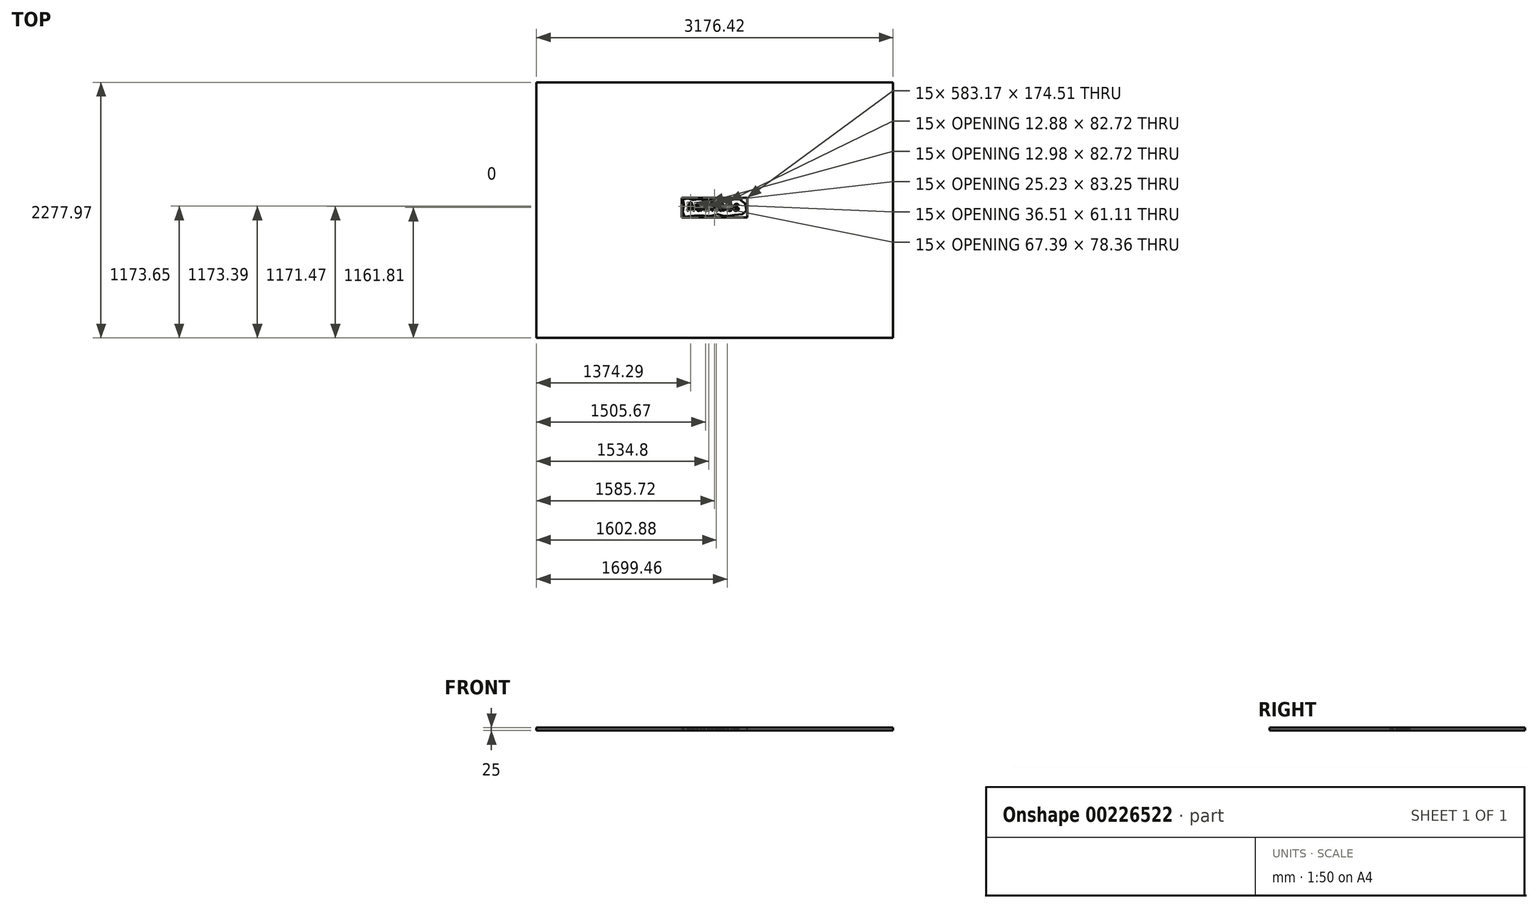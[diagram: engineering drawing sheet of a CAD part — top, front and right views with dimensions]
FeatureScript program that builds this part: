
annotation { "Feature Type Name" : "Feature", "Feature Type Description" : "" }
export const myFeature = defineFeature(function(context is Context, id is Id, definition is map)
    precondition{}
    {
        {
            var Q0;
            Q0=qCreatedBy(makeId("Top.planeOp"),FACE);
            var sketch = newSketch(context, id + "F0", { "sketchPlane" : qUnion([Q0])});
            skLineSegment(sketch, "E0.bottom", {"start": v(0, 0) * mm, "end": v(583.17, 0) * mm});
            skLineSegment(sketch, "E0.top", {"start": v(0, 174.5) * mm, "end": v(583.17, 174.5) * mm});
            skLineSegment(sketch, "E0.left", {"start": v(0, 0) * mm, "end": v(0, 174.5) * mm});
            skLineSegment(sketch, "E0.right", {"start": v(583.17, 0) * mm, "end": v(583.17, 174.5) * mm});
            skSolve(sketch);
        }
        {
            var Q0;
            Q0=qCreatedBy(makeId("Top.planeOp"),FACE);
            var sketch = newSketch(context, id + "F1", { "sketchPlane" : qUnion([Q0])});
            skText(sketch, "E1", { "text": "Audilabs", "fontName": "AllertaStencil-Regular.ttf"});
            const initialGuessF1  = {"E1": [0.03974, 0.05773, 1, 0, 0.0785]};
            skSetInitialGuess(sketch, initialGuessF1);
            skSolve(sketch);
        }
        {
            var Q0;
            Q0=makeQuery(id+"F0.imprint","IMPRINT",FACE,{"disambiguationData":[TD([[makeQuery(id+"F0.imprint","IMPRINT",EDGE,{"derivedFrom":sQuery(id+"F0.wireOp",EDGE,"E0.bottom")}),1.0]])]});
            extrude(context, id + "F2", {"entities" : qUnion([Q0]), "depth" : 25 * mm});
        }
        {
            var Q0;
            Q0 = qSketchRegion(id + "F1", true);
            var Q1;
            Q1=makeQuery(id+"F1.imprint","IMPRINT",FACE,{"disambiguationData":[TD([[makeQuery(id+"F1.imprint","IMPRINT",EDGE,{"derivedFrom":sQuery(id+"F1.wireOp",EDGE,"E1.sketch_text.stroke-213")}),-1.0]])]});
            var Q2;
            Q2=makeQuery(id+"F1.imprint","IMPRINT",FACE,{"disambiguationData":[TD([[makeQuery(id+"F1.imprint","IMPRINT",EDGE,{"derivedFrom":sQuery(id+"F1.wireOp",EDGE,"E1.sketch_text.stroke-204")}),-1.0]])]});
            var Q3;
            Q3=makeQuery(id+"F1.imprint","IMPRINT",FACE,{"disambiguationData":[TD([[makeQuery(id+"F1.imprint","IMPRINT",EDGE,{"derivedFrom":sQuery(id+"F1.wireOp",EDGE,"E1.sketch_text.stroke-184")}),-1.0]])]});
            var Q4;
            Q4=makeQuery(id+"F1.imprint","IMPRINT",FACE,{"disambiguationData":[TD([[makeQuery(id+"F1.imprint","IMPRINT",EDGE,{"derivedFrom":sQuery(id+"F1.wireOp",EDGE,"E1.sketch_text.stroke-198")}),-1.0]])]});
            var Q5;
            Q5=makeQuery(id+"F1.imprint","IMPRINT",FACE,{"disambiguationData":[TD([[makeQuery(id+"F1.imprint","IMPRINT",EDGE,{"derivedFrom":sQuery(id+"F1.wireOp",EDGE,"E1.sketch_text.stroke-0")}),-1.0]])]});
            var Q6;
            Q6=makeQuery(id+"F1.imprint","IMPRINT",FACE,{"disambiguationData":[TD([[makeQuery(id+"F1.imprint","IMPRINT",EDGE,{"derivedFrom":sQuery(id+"F1.wireOp",EDGE,"E1.sketch_text.stroke-7")}),-1.0]])]});
            var Q7;
            Q7=makeQuery(id+"F1.imprint","IMPRINT",FACE,{"disambiguationData":[TD([[makeQuery(id+"F1.imprint","IMPRINT",EDGE,{"derivedFrom":sQuery(id+"F1.wireOp",EDGE,"E1.sketch_text.stroke-11")}),-1.0]])]});
            var Q8;
            Q8=makeQuery(id+"F1.imprint","IMPRINT",FACE,{"disambiguationData":[TD([[makeQuery(id+"F1.imprint","IMPRINT",EDGE,{"derivedFrom":sQuery(id+"F1.wireOp",EDGE,"E1.sketch_text.stroke-31")}),-1.0]])]});
            var Q9;
            Q9=makeQuery(id+"F1.imprint","IMPRINT",FACE,{"disambiguationData":[TD([[makeQuery(id+"F1.imprint","IMPRINT",EDGE,{"derivedFrom":sQuery(id+"F1.wireOp",EDGE,"E1.sketch_text.stroke-36")}),-1.0]])]});
            var Q10;
            Q10=makeQuery(id+"F1.imprint","IMPRINT",FACE,{"disambiguationData":[TD([[makeQuery(id+"F1.imprint","IMPRINT",EDGE,{"derivedFrom":sQuery(id+"F1.wireOp",EDGE,"E1.sketch_text.stroke-41")}),-1.0]])]});
            var Q11;
            Q11=makeQuery(id+"F1.imprint","IMPRINT",FACE,{"disambiguationData":[TD([[makeQuery(id+"F1.imprint","IMPRINT",EDGE,{"derivedFrom":sQuery(id+"F1.wireOp",EDGE,"E1.sketch_text.stroke-66")}),-1.0]])]});
            var Q12;
            Q12=makeQuery(id+"F1.imprint","IMPRINT",FACE,{"disambiguationData":[TD([[makeQuery(id+"F1.imprint","IMPRINT",EDGE,{"derivedFrom":sQuery(id+"F1.wireOp",EDGE,"E1.sketch_text.stroke-70")}),-1.0]])]});
            var Q13;
            Q13=makeQuery(id+"F1.imprint","IMPRINT",FACE,{"disambiguationData":[TD([[makeQuery(id+"F1.imprint","IMPRINT",EDGE,{"derivedFrom":sQuery(id+"F1.wireOp",EDGE,"E1.sketch_text.stroke-78")}),-1.0]])]});
            var Q14;
            Q14=makeQuery(id+"F1.imprint","IMPRINT",FACE,{"disambiguationData":[TD([[makeQuery(id+"F1.imprint","IMPRINT",EDGE,{"derivedFrom":sQuery(id+"F1.wireOp",EDGE,"E1.sketch_text.stroke-96")}),-1.0]])]});
            var Q15;
            Q15=makeQuery(id+"F1.imprint","IMPRINT",FACE,{"disambiguationData":[TD([[makeQuery(id+"F1.imprint","IMPRINT",EDGE,{"derivedFrom":sQuery(id+"F1.wireOp",EDGE,"E1.sketch_text.stroke-115")}),-1.0]])]});
            var Q16;
            Q16=makeQuery(id+"F1.imprint","IMPRINT",FACE,{"disambiguationData":[TD([[makeQuery(id+"F1.imprint","IMPRINT",EDGE,{"derivedFrom":sQuery(id+"F1.wireOp",EDGE,"E1.sketch_text.stroke-151")}),-1.0]])]});
            var Q17;
            Q17=makeQuery(id+"F1.imprint","IMPRINT",FACE,{"disambiguationData":[TD([[makeQuery(id+"F1.imprint","IMPRINT",EDGE,{"derivedFrom":sQuery(id+"F1.wireOp",EDGE,"E1.sketch_text.stroke-157")}),-1.0]])]});
            extrude(context, id + "F3", {"entities" : qUnion([Q0, Q1, Q2, Q3, Q4, Q5, Q6, Q7, Q8, Q9, Q10, Q11, Q12, Q13, Q14, Q15, Q16, Q17]), "operationType" : NewBodyOperationType.REMOVE, "depth" : 25 * mm});
        }
        {
            var Q0;
            Q0=qCreatedBy(makeId("Top.planeOp"),FACE);
            var sketch = newSketch(context, id + "F4", { "sketchPlane" : qUnion([Q0])});
            skFitSpline(sketch, "E2", {"points": [v(59.71, 167.85) * mm, v(100.76, 153.6) * mm, v(164.26, 162.11) * mm, v(241.18, 149.67) * mm, v(283.16, 168.16) * mm, v(343.27, 156.9) * mm, v(463.41, 163) * mm, v(553.92, 138.65) * mm, v(575.11, 55.52) * mm, v(528.77, 23.78) * mm, v(428.45, 18.48) * mm, v(389.31, 5.7) * mm, v(336.13, 28.44) * mm, v(249.45, 10.01) * mm, v(144.76, 18.85) * mm, v(8.26, 13.37) * mm, v(20.37, 100.07) * mm, v(6.74, 156.56) * mm, v(59.71, 167.85) * mm]});
            skLineSegment(sketch, "E3.bottom", {"start": v(0, 0) * mm, "end": v(583.17, 0) * mm});
            skLineSegment(sketch, "E3.top", {"start": v(0, 174.5) * mm, "end": v(583.17, 174.5) * mm});
            skLineSegment(sketch, "E3.left", {"start": v(0, 0) * mm, "end": v(0, 174.5) * mm});
            skLineSegment(sketch, "E3.right", {"start": v(583.17, 0) * mm, "end": v(583.17, 174.5) * mm});
            skLineSegment(sketch, "E4.bottom", {"start": v(-1294.14, 1203.4) * mm, "end": v(1882.28, 1203.4) * mm});
            skLineSegment(sketch, "E4.top", {"start": v(-1294.14, -1074.56) * mm, "end": v(1882.28, -1074.56) * mm});
            skLineSegment(sketch, "E4.left", {"start": v(-1294.14, 1203.4) * mm, "end": v(-1294.14, -1074.56) * mm});
            skLineSegment(sketch, "E4.right", {"start": v(1882.28, 1203.4) * mm, "end": v(1882.28, -1074.56) * mm});
            skSolve(sketch);
        }
        {
            var Q0;
            {var subQ4=sQuery(id+"F4.wireOp",EDGE,"E3.bottom");Q0=makeQuery(id+"F4.imprint","IMPRINT",FACE,{"disambiguationData":[TD([[makeQuery(id+"F4.imprint","IMPRINT",EDGE,{"derivedFrom":subQ4}),1.0]])]});}
            extrude(context, id + "F5", {"entities" : qUnion([Q0]), "operationType" : NewBodyOperationType.REMOVE, "depth" : 25 * mm});
        }
        {
            var Q0;
            {var subQ1=sQuery(id+"F4.wireOp",EDGE,"E3.bottom");Q0=makeQuery(id+"F4.imprint","IMPRINT",FACE,{"disambiguationData":[TD([[makeQuery(id+"F4.imprint","IMPRINT",EDGE,{"derivedFrom":subQ1}),-1.0]])]});}
            extrude(context, id + "F6", {"entities" : qUnion([Q0]), "depth" : 25 * mm});
        }
    });
